SOLIDWORKS PART (.sldprt)
format: sldprt  version: not decoded by parser v0  size: 1,378,304 bytes
history: native  units: mm
features: sketch x5, plane x4, sweep x2, material x1, revolve x1, helix x1 (+8 scaffold rows collapsed)
feature tree (22):
  scaffold x8  (default folders/planes/origin — collapsed)
  material  "Messing"
  plane  "Ebene vorne"
  plane  "Ebene oben"
  plane  "Ebene rechts"
  sketch  "Skizze1"  dims[D1=1000.0mm D2=5.0mm]
  revolve  "Rotation1"  Angle=360deg
  sketch  "Skizze2"  dims[D1=0.0mm]
  helix  "Spirale/Helix1"  Pitch=500mm
  sketch  "Skizze3"  dims[c1.D2=~0.133333mm c1.D1=~1.56448mm c2.D1=60.0deg c2.D3=0.8mm c2.D4=0.1mm]
  sweep  "Schnitt-Austragung1"
  plane  "Ebene1"  Offset=500mm
  sketch  "Skizze4"  dims[D1=5.0mm Spirale/Helix2=0.0 D3=504.0mm D4=0.8mm D5=630000.0mm D7=90.0deg]
  sketch  "Skizze5"  dims[D1=0.0mm]
  sweep  "Schnitt-Austragung2"
decode coverage: 7 of 9 modeling features carry decoded parameters
note: ~ marks probable driven/reference dimensions
note: suppression state not decoded; provenance and decode notes live in map.json
